# Revit family: Sink-Drop_In-Kohler-2196X
name_source: partatom
category: Plumbing Fixtures
revit_build: Autodesk Revit MEP 2012 (Build: 20110916_2132(x64)
units: mm (PartAtom-declared; Revit-internal decimal feet)

## types (6) — shared parameters
Date Modified = January 26, 2015
Description = See Part Description
Equipment Abbreviation = SK
Family Version = 1.0
Manufacturer = Kohler Company
Model = See Part Number
Model Disclaimer = Contact Kohler Company For More Information
Product Page URL = http://www.us.kohler.com
URL = http://www.us.kohler.com

## per-type parameters (varying)
| type | Product Material | zz Integer 1 |
| White | Vitreous China - Kohler - White | 1 |
| Biscuit | Vitreous China - Kohler - Biscuit | 3 |
| Almond | Vitreous China - Kohler - Almond | 4 |
| Dune | Vitreous China - Kohler - Dune | 6 |
| Ice Grey | Vitreous China - Kohler - Ice Grey | 7 |
| Black | Vitreous China - Kohler - Black | 16 |

## geometry (parser evidence)
native form markers: Blend x6, Sweep x1
no freeform markers — native parametric forms only
